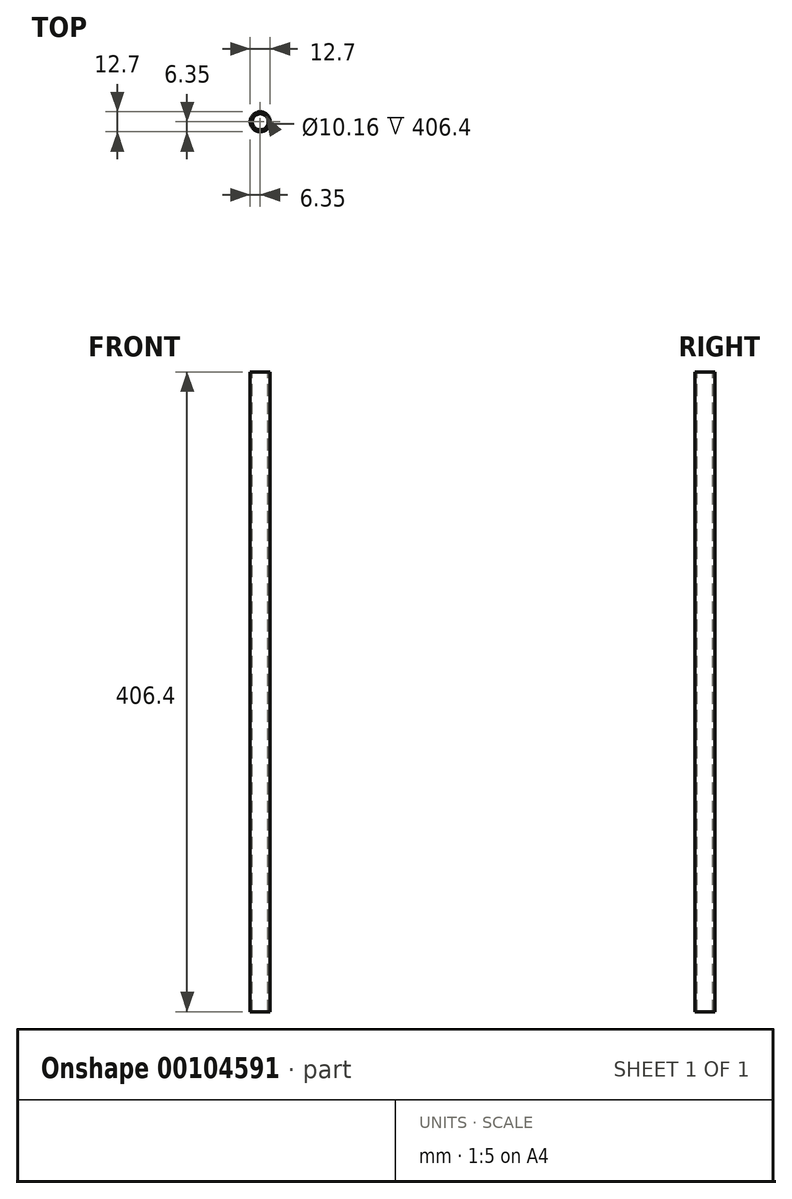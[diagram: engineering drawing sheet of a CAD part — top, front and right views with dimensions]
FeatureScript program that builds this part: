
annotation { "Feature Type Name" : "Feature", "Feature Type Description" : "" }
export const myFeature = defineFeature(function(context is Context, id is Id, definition is map)
    precondition{}
    {
        {
            var Q0;
            Q0=qCreatedBy(makeId("Top.planeOp"),FACE);
            var sketch = newSketch(context, id + "F0", { "sketchPlane" : qUnion([Q0])});
            skCircle(sketch, "E0", {"center": v(0, 0) * mm, "radius": 6.35 * mm});
            skCircle(sketch, "E1", {"center": v(0, 0) * mm, "radius": 5.08 * mm});
            skSolve(sketch);
        }
        {
            var Q0;
            Q0=qCreatedBy(makeId("Front.planeOp"),FACE);
            var sketch = newSketch(context, id + "F1", { "sketchPlane" : qUnion([Q0])});
            skLineSegment(sketch, "E2", {"start": v(0, 0) * mm, "end": v(0, 406.4) * mm});
            skSolve(sketch);
        }
        {
            var Q0;
            Q0=makeQuery(id+"F0.imprint","IMPRINT",FACE,{"disambiguationData":[TD([[makeQuery(id+"F0.imprint","IMPRINT",EDGE,{"derivedFrom":sQuery(id+"F0.wireOp",EDGE,"E0")}),1.0]])]});
            var Q1;
            Q1=sQuery(id+"F1.wireOp",EDGE,"E2");
            sweep(context, id + "F2", {"profiles" : qUnion([Q0]), "path" : qUnion([Q1])});
        }
    });
